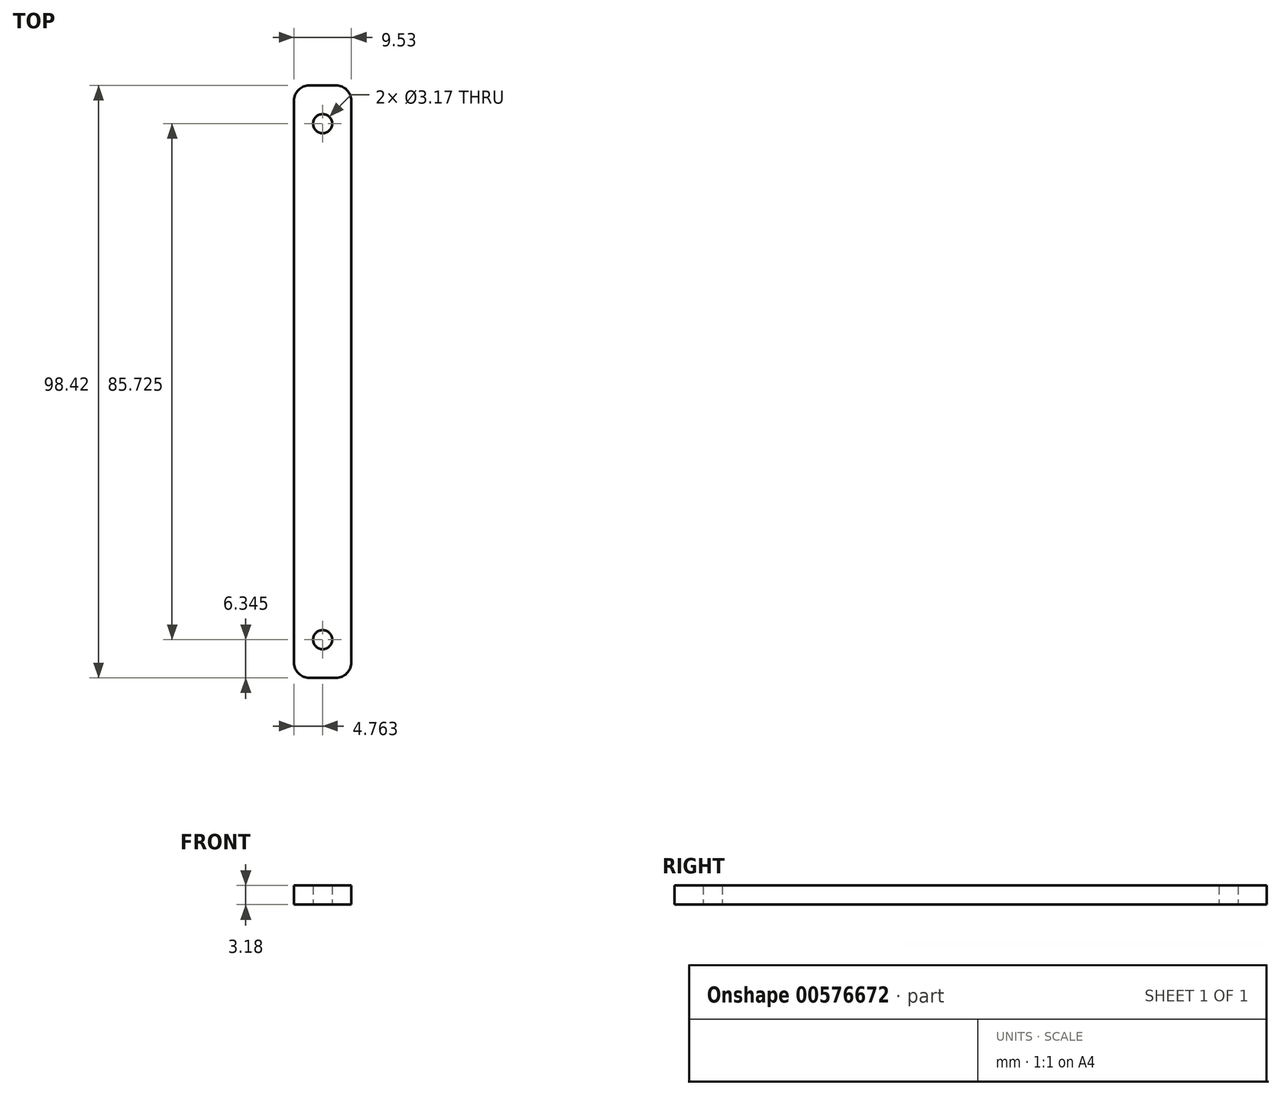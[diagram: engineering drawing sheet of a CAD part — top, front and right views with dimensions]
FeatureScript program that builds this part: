
annotation { "Feature Type Name" : "Feature", "Feature Type Description" : "" }
export const myFeature = defineFeature(function(context is Context, id is Id, definition is map)
    precondition{}
    {
        {
            var Q0;
            Q0=qCreatedBy(makeId("Top.planeOp"),FACE);
            var sketch = newSketch(context, id + "F0", { "sketchPlane" : qUnion([Q0])});
            skLineSegment(sketch, "E0.bottom", {"start": v(2.54, 0) * mm, "end": v(6.99, 0) * mm});
            skLineSegment(sketch, "E0.top", {"start": v(2.54, -98.43) * mm, "end": v(6.99, -98.43) * mm});
            skLineSegment(sketch, "E0.left", {"start": v(0, -2.54) * mm, "end": v(0, -95.89) * mm});
            skLineSegment(sketch, "E0.right", {"start": v(9.53, -2.54) * mm, "end": v(9.53, -95.89) * mm});
            skCircle(sketch, "E1", {"center": v(4.76, -6.35) * mm, "radius": 1.59 * mm});
            skLineSegment(sketch, "E2", {"start": v(0, -49.21) * mm, "end": v(4.76, -49.21) * mm, "construction": true});
            skCircle(sketch, "E3.MirrorC", {"center": v(4.76, -92.08) * mm, "radius": 1.59 * mm});
            skPoint(sketch, "E4.visualSharp", {"position": v(0, -98.43) * mm});
            skArc(sketch, "E4.filletArc", {"start": v(0, -95.89) * mm, "mid": v(0.74, -97.68) * mm, "end": v(2.54, -98.43) * mm});
            skPoint(sketch, "E5.visualSharp", {"position": v(9.53, -98.43) * mm});
            skArc(sketch, "E5.filletArc", {"start": v(6.99, -98.43) * mm, "mid": v(8.78, -97.68) * mm, "end": v(9.53, -95.89) * mm});
            skPoint(sketch, "E6.visualSharp", {"position": v(9.53, 0) * mm});
            skArc(sketch, "E6.filletArc", {"start": v(9.53, -2.54) * mm, "mid": v(8.78, -0.74) * mm, "end": v(6.99, 0) * mm});
            skPoint(sketch, "E7.visualSharp", {"position": v(0, 0) * mm});
            skArc(sketch, "E7.filletArc", {"start": v(2.54, 0) * mm, "mid": v(0.74, -0.74) * mm, "end": v(0, -2.54) * mm});
            skSolve(sketch);
        }
        {
            var Q0;
            Q0=makeQuery(id+"F0.imprint","IMPRINT",FACE,{"disambiguationData":[TD([[makeQuery(id+"F0.imprint","IMPRINT",EDGE,{"derivedFrom":sQuery(id+"F0.wireOp",EDGE,"E0.bottom")}),-1.0]])]});
            extrude(context, id + "F1", {"entities" : qUnion([Q0]), "depth" : 3.17 * mm, "offsetDistance" : 25.4 * mm});
        }
    });
